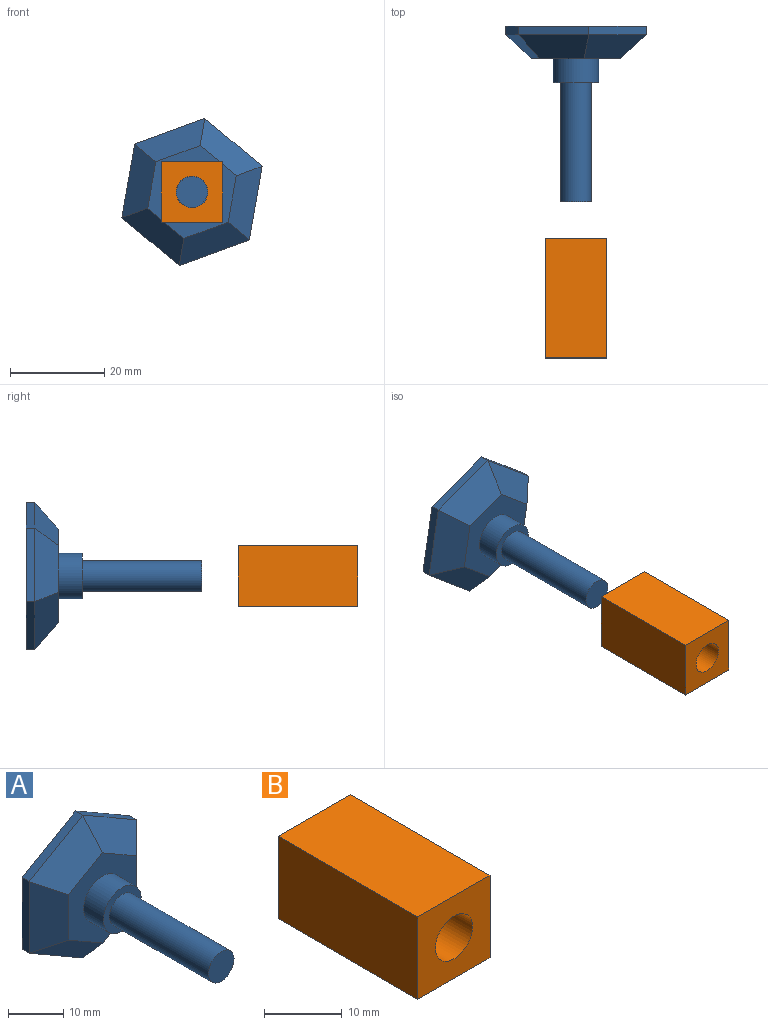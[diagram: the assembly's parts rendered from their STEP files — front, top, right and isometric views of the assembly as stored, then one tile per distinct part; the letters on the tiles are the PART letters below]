
ASSEMBLY  parts=2 mates=1
PART A: 18 faces, bbox 27.5x37.4x31.8 mm
  f0: plane 13.76x7.95mm, normal (0.5,0,-0.87), area 29.1mm2, adj f1,f5,f7,f10
  f1: plane 15.89x1.83mm, normal (1,0,0), area 29.1mm2, adj f0,f2,f7,f11
  f2: plane 13.76x7.95mm, normal (0.5,0,0.87), area 29.1mm2, adj f1,f3,f7,f13
  f3: plane 13.76x7.95mm, normal (-0.5,0,0.87), area 29.1mm2, adj f2,f4,f7,f15
  f4: plane 15.89x1.83mm, normal (-1,0,0), area 29.1mm2, adj f3,f5,f7,f14
  f5: plane 13.76x7.95mm, normal (-0.5,0,-0.87), area 29.1mm2, adj f0,f4,f7,f12
  f6: plane 20.05x17.36mm, normal (0,-1,0), area 187.2mm2, adj f8,f10,f11,f12,f13,f14,f15
  f7: plane 31.78x27.52mm, normal (0,1,0), area 656mm2, adj f0,f1,f2,f3,f4,f5
  f8: cylinder r=4.85mm len=9.7mm, axis (0,1,0), area 154.5mm2, adj f6,f9
  f9: plane 9.7x9.7mm, normal (0,-1,0), area 39.7mm2, adj f8,f16
  f10: plane 13.76x10.88mm, normal (0.35,-0.71,-0.61), area 93.1mm2, adj f0,f6,f11,f12
  f11: plane 15.89x5.08mm, normal (0.71,-0.71,0), area 93.1mm2, adj f1,f6,f10,f13
  f12: plane 13.76x10.88mm, normal (-0.35,-0.71,-0.61), area 93.1mm2, adj f5,f6,f10,f14
  f13: plane 13.76x10.88mm, normal (0.35,-0.71,0.61), area 93.1mm2, adj f2,f6,f11,f15
  f14: plane 15.89x5.08mm, normal (-0.71,-0.71,0), area 93.1mm2, adj f4,f6,f12,f15
  f15: plane 13.76x10.88mm, normal (-0.35,-0.71,0.61), area 93.1mm2, adj f3,f6,f13,f14
  f16: cylinder r=3.3mm len=25.4mm, axis (0,1,0), area 526.7mm2, adj f9,f17
  f17: plane 6.6x6.6mm, normal (0,-1,0), area 34.2mm2, adj f16
PART B: 7 faces, bbox 13.1x25.4x12.9 mm
  f0: plane 25.4x12.95mm, normal (1,0,0), area 328.9mm2, adj f1,f3,f5,f6
  f1: plane 25.4x13.06mm, normal (0,0,1), area 331.8mm2, adj f0,f2,f5,f6
  f2: plane 25.4x12.95mm, normal (-1,0,0), area 328.9mm2, adj f1,f3,f5,f6
  f3: plane 25.4x13.06mm, normal (0,0,-1), area 331.8mm2, adj f0,f2,f5,f6
  f4: cylinder r=3.37mm len=25.4mm, axis (0,1,0), area 537.1mm2, adj f5,f6
  f5: plane 13.06x12.95mm, normal (0,-1,0), area 133.6mm2, adj f0,f1,f2,f3,f4
  f6: plane 13.06x12.95mm, normal (0,1,0), area 133.6mm2, adj f0,f1,f2,f3,f4
PLACE A rot(axis=(0,1,0),69.9deg) t=(0,7.77,0)mm
PLACE B at identity fixed
MATE cylindrical A.f16 <-> B.f4  axis (0,1,0) through (0,-16.91,0)mm
